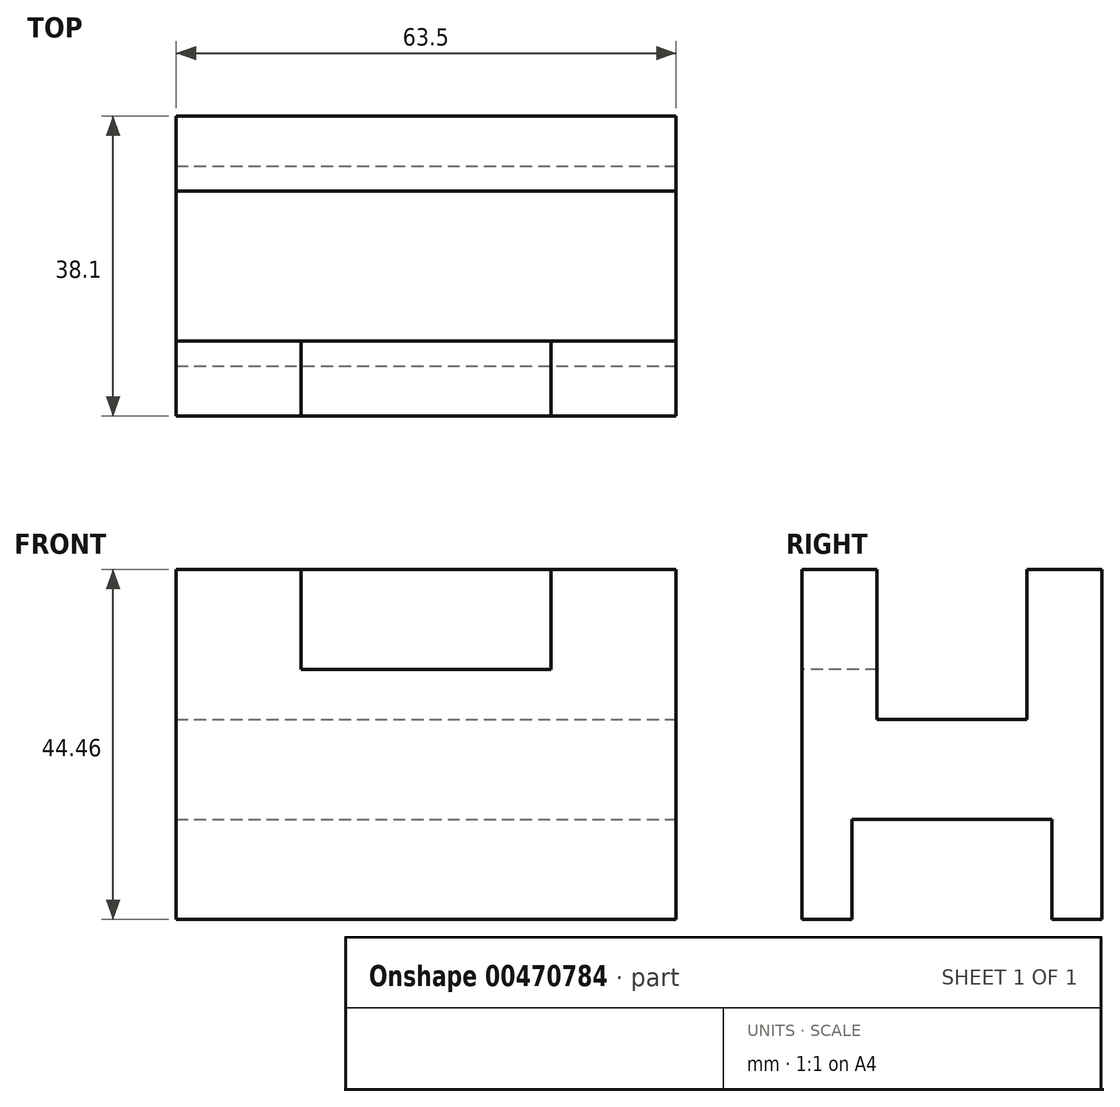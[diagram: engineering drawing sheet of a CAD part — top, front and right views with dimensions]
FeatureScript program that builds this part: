
annotation { "Feature Type Name" : "Feature", "Feature Type Description" : "" }
export const myFeature = defineFeature(function(context is Context, id is Id, definition is map)
    precondition{}
    {
        {
            var Q0;
            Q0=qCreatedBy(makeId("Front.planeOp"),FACE);
            var sketch = newSketch(context, id + "F0", { "sketchPlane" : qUnion([Q0])});
            skLineSegment(sketch, "E0.bottom", {"start": v(31.75, -22.23) * mm, "end": v(-31.75, -22.23) * mm});
            skLineSegment(sketch, "E0.top", {"start": v(31.75, 22.23) * mm, "end": v(-31.75, 22.23) * mm});
            skLineSegment(sketch, "E0.left", {"start": v(31.75, -22.23) * mm, "end": v(31.75, 22.23) * mm});
            skLineSegment(sketch, "E0.right", {"start": v(-31.75, -22.23) * mm, "end": v(-31.75, 22.23) * mm});
            skPoint(sketch, "E0.middle", {"position": v(0, 0) * mm});
            skSolve(sketch);
        }
        {
            var Q0;
            Q0 = qSketchRegion(id + "F0", true);
            extrude(context, id + "F1", {"entities" : qUnion([Q0]), "depth" : 38.1 * mm});
        }
        {
            var Q0;
            Q0=makeQuery(id+"F1.opExtrude","CAP_FACE",FACE,{"disambiguationData":[OSD([sQuery(id+"F0.wireOp",EDGE,"E0.bottom"),sQuery(id+"F0.wireOp",EDGE,"E0.top"),sQuery(id+"F0.wireOp",EDGE,"E0.left"),sQuery(id+"F0.wireOp",EDGE,"E0.right")])],"isStart":false});
            var sketch = newSketch(context, id + "F2", { "sketchPlane" : qUnion([Q0])});
            skLineSegment(sketch, "E1.bottom", {"start": v(-15.88, 22.23) * mm, "end": v(15.88, 22.23) * mm});
            skLineSegment(sketch, "E1.top", {"start": v(-15.88, 9.53) * mm, "end": v(15.88, 9.53) * mm});
            skLineSegment(sketch, "E1.left", {"start": v(-15.88, 22.23) * mm, "end": v(-15.88, 9.53) * mm});
            skLineSegment(sketch, "E1.right", {"start": v(15.88, 22.23) * mm, "end": v(15.88, 9.53) * mm});
            skSolve(sketch);
        }
        {
            var Q0;
            Q0 = qSketchRegion(id + "F2", true);
            extrude(context, id + "F3", {"entities" : qUnion([Q0]), "operationType" : NewBodyOperationType.REMOVE, "oppositeDirection" : true, "depth" : 9.52 * mm});
        }
        {
            var Q0;
            Q0=makeQuery(id+"F1.opExtrude","SWEPT_FACE",FACE,{"disambiguationData":[OSD([sQuery(id+"F0.wireOp",EDGE,"E0.left")])]});
            var sketch = newSketch(context, id + "F4", { "sketchPlane" : qUnion([Q0])});
            skLineSegment(sketch, "E2.bottom", {"start": v(-28.58, 22.23) * mm, "end": v(-9.53, 22.23) * mm});
            skLineSegment(sketch, "E2.top", {"start": v(-28.58, 3.18) * mm, "end": v(-9.53, 3.18) * mm});
            skLineSegment(sketch, "E2.left", {"start": v(-28.58, 22.23) * mm, "end": v(-28.58, 3.18) * mm});
            skLineSegment(sketch, "E2.right", {"start": v(-9.53, 22.23) * mm, "end": v(-9.53, 3.18) * mm});
            skSolve(sketch);
        }
        {
            var Q0;
            Q0 = qSketchRegion(id + "F4", true);
            extrude(context, id + "F5", {"entities" : qUnion([Q0]), "operationType" : NewBodyOperationType.REMOVE, "endBound" : BoundingType.THROUGH_ALL, "oppositeDirection" : true, "depth" : 25.4 * mm});
        }
        {
            var Q0;
            Q0=makeQuery(id+"F1.opExtrude","SWEPT_FACE",FACE,{"disambiguationData":[OSD([sQuery(id+"F0.wireOp",EDGE,"E0.left")])]});
            var sketch = newSketch(context, id + "F6", { "sketchPlane" : qUnion([Q0])});
            skLineSegment(sketch, "E3.bottom", {"start": v(-31.75, -22.22) * mm, "end": v(-6.35, -22.22) * mm});
            skLineSegment(sketch, "E3.top", {"start": v(-31.75, -9.52) * mm, "end": v(-6.35, -9.52) * mm});
            skLineSegment(sketch, "E3.left", {"start": v(-31.75, -22.22) * mm, "end": v(-31.75, -9.52) * mm});
            skLineSegment(sketch, "E3.right", {"start": v(-6.35, -22.22) * mm, "end": v(-6.35, -9.52) * mm});
            skSolve(sketch);
        }
        {
            var Q0;
            Q0 = qSketchRegion(id + "F6", true);
            extrude(context, id + "F7", {"entities" : qUnion([Q0]), "operationType" : NewBodyOperationType.REMOVE, "endBound" : BoundingType.THROUGH_ALL, "oppositeDirection" : true, "depth" : 25.4 * mm});
        }
    });
